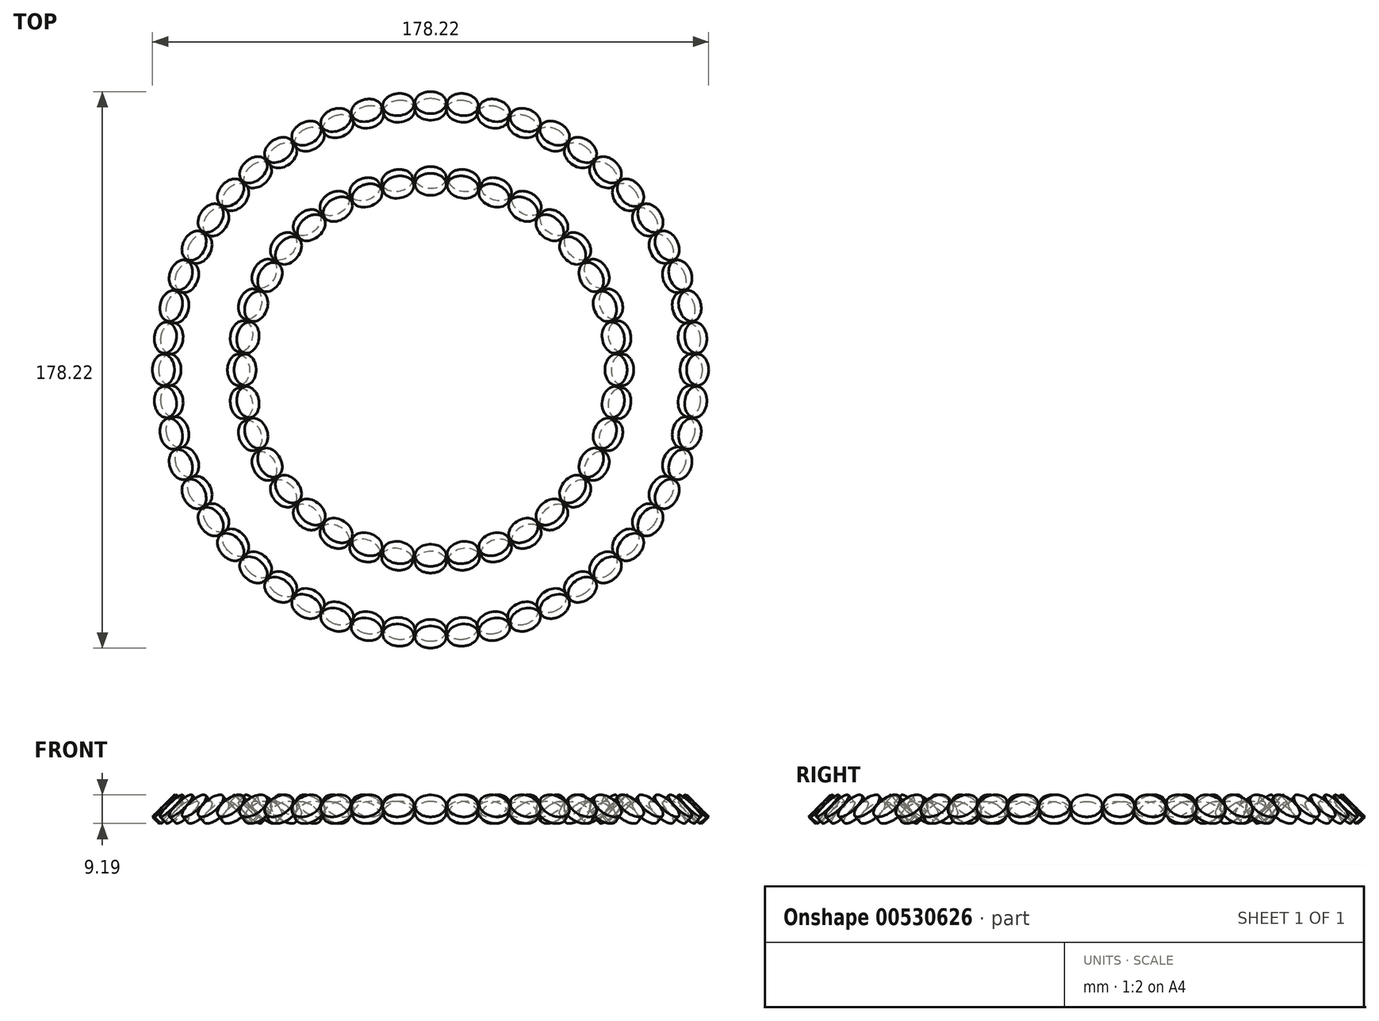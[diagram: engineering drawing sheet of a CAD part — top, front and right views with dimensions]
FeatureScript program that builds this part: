
annotation { "Feature Type Name" : "Feature", "Feature Type Description" : "" }
export const myFeature = defineFeature(function(context is Context, id is Id, definition is map)
    precondition{}
    {
        {
            var Q0;
            Q0=qCreatedBy(makeId("Front.planeOp"),FACE);
            var sketch = newSketch(context, id + "F0", { "sketchPlane" : qUnion([Q0])});
            skLineSegment(sketch, "E0", {"start": v(-90.33, 0) * mm, "end": v(-54.67, 0) * mm});
            skLineSegment(sketch, "E1", {"start": v(-54.67, 0) * mm, "end": v(-65.33, 10.65) * mm});
            skLineSegment(sketch, "E2", {"start": v(-65.33, 10.65) * mm, "end": v(-79.67, 10.65) * mm});
            skLineSegment(sketch, "E3", {"start": v(-79.67, 10.65) * mm, "end": v(-90.33, 0) * mm});
            skLineSegment(sketch, "E4", {"start": v(0, 0) * mm, "end": v(0, 33.08) * mm, "construction": true});
            skPoint(sketch, "E5", {"position": v(-60, 5.33) * mm});
            skPoint(sketch, "E6", {"position": v(-85, 5.33) * mm});
            skPoint(sketch, "E7", {"position": v(-72.5, 10.65) * mm});
            skPoint(sketch, "E8", {"position": v(-72.5, 20.65) * mm});
            skLineSegment(sketch, "E9", {"start": v(-81.09, 9.24) * mm, "end": v(-79.92, 8.07) * mm});
            skLineSegment(sketch, "E10", {"start": v(-79.92, 8.07) * mm, "end": v(-87, 1) * mm});
            skLineSegment(sketch, "E11", {"start": v(-87, 1) * mm, "end": v(-88.16, 2.17) * mm});
            skLineSegment(sketch, "E12", {"start": v(-72.5, 10.65) * mm, "end": v(-72.5, 0) * mm, "construction": true});
            skLineSegment(sketch, "E13.MirrorCS", {"start": v(-58, 1) * mm, "end": v(-56.84, 2.17) * mm});
            skLineSegment(sketch, "E14.MirrorCS", {"start": v(-63.91, 9.24) * mm, "end": v(-65.08, 8.07) * mm});
            skLineSegment(sketch, "E15.MirrorCS", {"start": v(-65.08, 8.07) * mm, "end": v(-58, 1) * mm});
            skLineSegment(sketch, "E16", {"start": v(-83.46, 4.54) * mm, "end": v(-84.62, 5.7) * mm});
            skLineSegment(sketch, "E17", {"start": v(-61.54, 4.54) * mm, "end": v(-60.38, 5.7) * mm});
            skLineSegment(sketch, "E18", {"start": v(-88.16, 2.17) * mm, "end": v(-89.11, 3.12) * mm});
            skLineSegment(sketch, "E19", {"start": v(-89.11, 3.12) * mm, "end": v(-82.04, 10.2) * mm});
            skLineSegment(sketch, "E20", {"start": v(-82.04, 10.2) * mm, "end": v(-81.09, 9.24) * mm});
            skLineSegment(sketch, "E21.MirrorCS", {"start": v(-55.89, 3.12) * mm, "end": v(-62.96, 10.2) * mm});
            skLineSegment(sketch, "E22.MirrorCS", {"start": v(-62.96, 10.2) * mm, "end": v(-63.91, 9.24) * mm});
            skLineSegment(sketch, "E23.MirrorCS", {"start": v(-56.84, 2.17) * mm, "end": v(-55.89, 3.12) * mm});
            skLineSegment(sketch, "E24", {"start": v(-84.62, 5.7) * mm, "end": v(-85.58, 6.66) * mm});
            skLineSegment(sketch, "E25", {"start": v(-60.38, 5.7) * mm, "end": v(-59.42, 6.66) * mm});
            skSolve(sketch);
        }
        {
            var Q0;
            Q0=sQuery(id+"F0.wireOp",EDGE,"E4");
            var Q1;
            Q1=sQuery(id+"F0.wireOp",EDGE,"E1");
            var Q2;
            Q2=sQuery(id+"F0.wireOp",EDGE,"E3");
            var Q3;
            Q3=sQuery(id+"F0.wireOp",EDGE,"E2");
            var Q4;
            Q4=sQuery(id+"F0.wireOp",EDGE,"E0");
            var Q5;
            Q5=sQuery(id+"F0.wireOp",EDGE,"E4");
            revolve(context, id + "F1", {"bodyType" : ToolBodyType.SURFACE, "surfaceEntities" : qUnion([Q0, Q1, Q2, Q3, Q4]), "axis" : qUnion([Q5]), "revolveType" : RevolveType.FULL});
        }
        {
            var Q0;
            {var subQ0=sQuery(id+"F0.wireOp",EDGE,"E11");Q0=makeQuery(id+"F0.imprint","IMPRINT",FACE,{"disambiguationData":[TD([[makeQuery(id+"F0.imprint","IMPRINT",EDGE,{"derivedFrom":subQ0}),-1.0]])]});}
            var Q1;
            {var subQ0=sQuery(id+"F0.wireOp",EDGE,"E18");Q1=makeQuery(id+"F0.imprint","IMPRINT",FACE,{"disambiguationData":[TD([[makeQuery(id+"F0.imprint","IMPRINT",EDGE,{"derivedFrom":subQ0}),-1.0]])]});}
            var Q2;
            Q2=sQuery(id+"F0.wireOp",EDGE,"E16");
            revolve(context, id + "F2", {"entities" : qUnion([Q0, Q1]), "axis" : qUnion([Q2]), "revolveType" : RevolveType.FULL});
        }
        {
            var Q0;
            {var subQ0=sQuery(id+"F0.wireOp",EDGE,"E13.MirrorCS");Q0=makeQuery(id+"F0.imprint","IMPRINT",FACE,{"disambiguationData":[TD([[makeQuery(id+"F0.imprint","IMPRINT",EDGE,{"derivedFrom":subQ0}),1.0]])]});}
            var Q1;
            {var subQ0=sQuery(id+"F0.wireOp",EDGE,"E23.MirrorCS");Q1=makeQuery(id+"F0.imprint","IMPRINT",FACE,{"disambiguationData":[TD([[makeQuery(id+"F0.imprint","IMPRINT",EDGE,{"derivedFrom":subQ0}),1.0]])]});}
            var Q2;
            Q2=sQuery(id+"F0.wireOp",EDGE,"E17");
            revolve(context, id + "F3", {"entities" : qUnion([Q0, Q1]), "axis" : qUnion([Q2]), "revolveType" : RevolveType.FULL});
        }
        {
            var Q0;
            Q0=makeQuery(id+"F3.opRevolve","SWEPT_BODY",BODY,{"disambiguationData":[OSD([sQuery(id+"F0.wireOp",EDGE,"E13.MirrorCS"),sQuery(id+"F0.wireOp",EDGE,"E15.MirrorCS"),sQuery(id+"F0.wireOp",EDGE,"E17"),sQuery(id+"F0.wireOp",EDGE,"E21.MirrorCS"),sQuery(id+"F0.wireOp",EDGE,"E23.MirrorCS"),sQuery(id+"F0.wireOp",EDGE,"E25")])]});
            var Q1;
            Q1=sQuery(id+"F0.wireOp",EDGE,"E4");
            circularPattern(context, id + "F4", {"entities" : qUnion([Q0]), "axis" : qUnion([Q1]), "angle" : 360 * degree, "instanceCount" : 36, "equalSpace" : true});
        }
        {
            var Q0;
            Q0=makeQuery(id+"F2.opRevolve","SWEPT_BODY",BODY,{"disambiguationData":[OSD([sQuery(id+"F0.wireOp",EDGE,"E10"),sQuery(id+"F0.wireOp",EDGE,"E11"),sQuery(id+"F0.wireOp",EDGE,"E16"),sQuery(id+"F0.wireOp",EDGE,"E18"),sQuery(id+"F0.wireOp",EDGE,"E19"),sQuery(id+"F0.wireOp",EDGE,"E24")])]});
            var Q1;
            Q1=sQuery(id+"F0.wireOp",EDGE,"E4");
            circularPattern(context, id + "F5", {"entities" : qUnion([Q0]), "axis" : qUnion([Q1]), "angle" : 360 * degree, "instanceCount" : 52, "equalSpace" : true});
        }
    });
